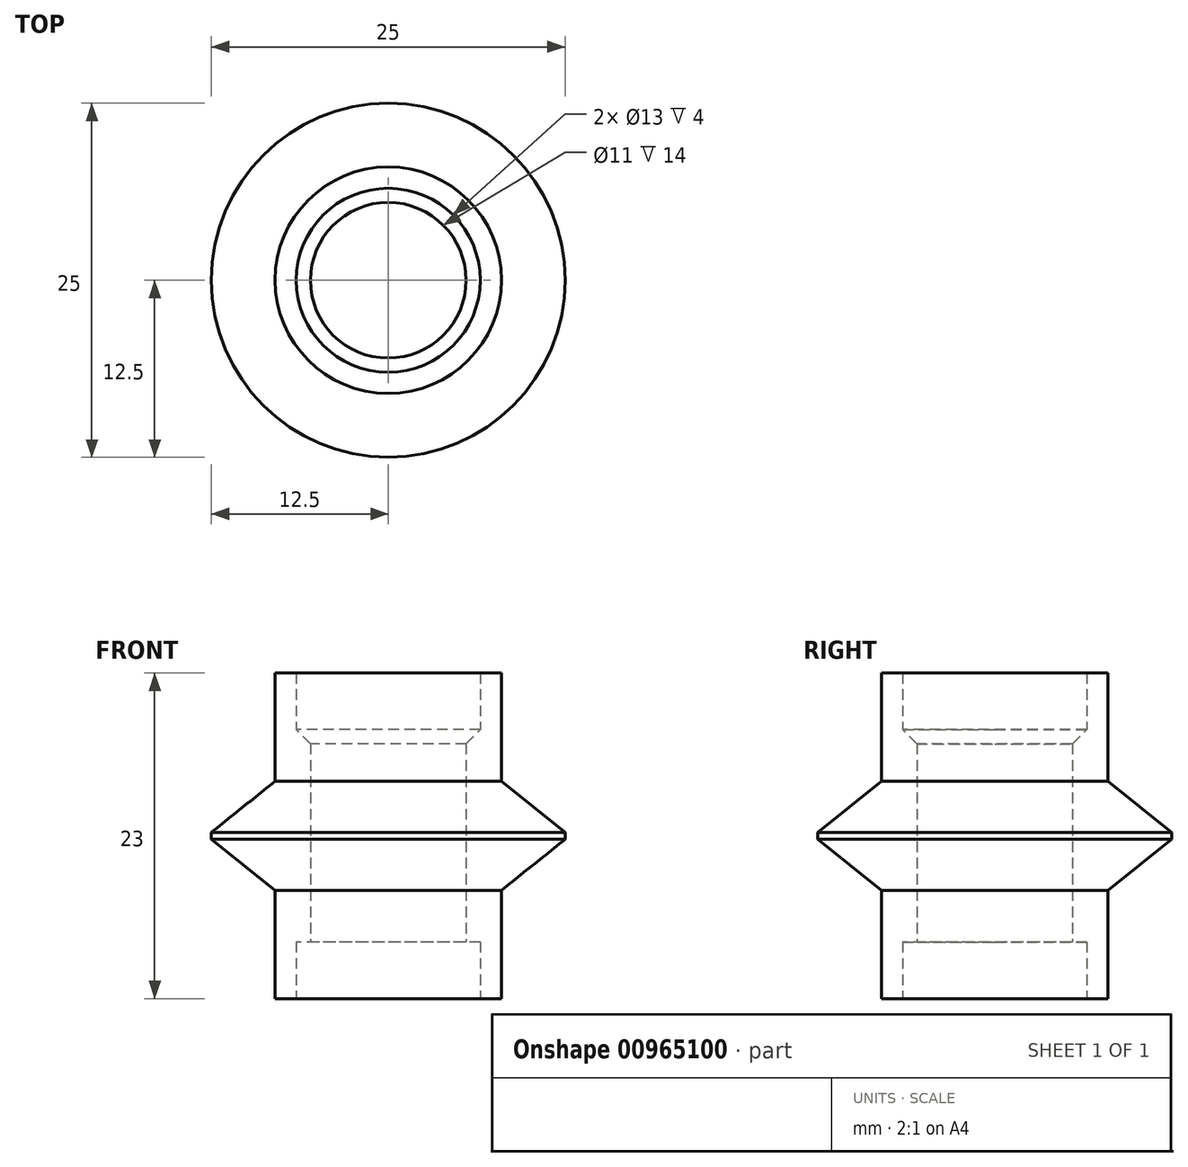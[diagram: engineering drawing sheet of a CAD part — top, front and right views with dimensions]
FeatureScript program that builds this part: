
annotation { "Feature Type Name" : "Feature", "Feature Type Description" : "" }
export const myFeature = defineFeature(function(context is Context, id is Id, definition is map)
    precondition{}
    {
        {
            var Q0;
            Q0=qCreatedBy(makeId("Top.planeOp"),FACE);
            var sketch = newSketch(context, id + "F0", { "sketchPlane" : qUnion([Q0])});
            skCircle(sketch, "E0", {"center": v(0, 0) * mm, "radius": 12.5 * mm});
            skCircle(sketch, "E1", {"center": v(0, 0) * mm, "radius": 8 * mm});
            skCircle(sketch, "E2", {"center": v(0, 0) * mm, "radius": 6.5 * mm});
            skCircle(sketch, "E3", {"center": v(0, 0) * mm, "radius": 5.5 * mm});
            skSolve(sketch);
        }
        {
            var Q0;
            Q0=makeQuery(id+"F0.imprint","IMPRINT",FACE,{"disambiguationData":[TD([[makeQuery(id+"F0.imprint","IMPRINT",EDGE,{"derivedFrom":sQuery(id+"F0.wireOp",EDGE,"E1")}),1.0]])]});
            extrude(context, id + "F1", {"entities" : qUnion([Q0]), "endBound" : BoundingType.SYMMETRIC, "depth" : 23 * mm, "offsetDistance" : 25 * mm});
        }
        {
            var Q0;
            Q0=makeQuery(id+"F0.imprint","IMPRINT",FACE,{"disambiguationData":[TD([[makeQuery(id+"F0.imprint","IMPRINT",EDGE,{"derivedFrom":sQuery(id+"F0.wireOp",EDGE,"E0")}),1.0]])]});
            extrude(context, id + "F2", {"entities" : qUnion([Q0]), "operationType" : NewBodyOperationType.ADD, "endBound" : BoundingType.SYMMETRIC, "depth" : 8.5 * mm, "offsetDistance" : 25 * mm});
        }
        {
            var Q0;
            Q0=makeQuery(id+"F2.opExtrude","CAP_EDGE",EDGE,{"disambiguationData":[OSD([sQuery(id+"F0.wireOp",EDGE,"E0")])],"isStart":false});
            chamfer(context, id + "F3", {"entities" : qUnion([Q0]), "chamferType" : ChamferType.TWO_OFFSETS, "width1" : 5 * mm, "oppositeDirection" : false, "width2" : 4 * mm, "tangentPropagation" : true});
        }
        {
            var Q0;
            Q0=makeQuery(id+"F2.opExtrude","CAP_EDGE",EDGE,{"disambiguationData":[OSD([sQuery(id+"F0.wireOp",EDGE,"E0")])],"isStart":true});
            chamfer(context, id + "F4", {"entities" : qUnion([Q0]), "chamferType" : ChamferType.TWO_OFFSETS, "width1" : 4 * mm, "oppositeDirection" : false, "width2" : 5 * mm, "tangentPropagation" : true});
        }
        {
            var Q0;
            Q0=makeQuery(id+"F0.imprint","IMPRINT",FACE,{"disambiguationData":[TD([[makeQuery(id+"F0.imprint","IMPRINT",EDGE,{"derivedFrom":sQuery(id+"F0.wireOp",EDGE,"E2")}),1.0]])]});
            extrude(context, id + "F5", {"entities" : qUnion([Q0]), "operationType" : NewBodyOperationType.ADD, "endBound" : BoundingType.SYMMETRIC, "depth" : 15 * mm, "offsetDistance" : 25 * mm});
        }
        {
            var Q0;
            Q0=makeQuery(id+"F5.opExtrude","CAP_EDGE",EDGE,{"disambiguationData":[OSD([sQuery(id+"F0.wireOp",EDGE,"E3")])],"isStart":false});
            chamfer(context, id + "F6", {"entities" : qUnion([Q0]), "width" : 1 * mm, "tangentPropagation" : true});
        }
    });
